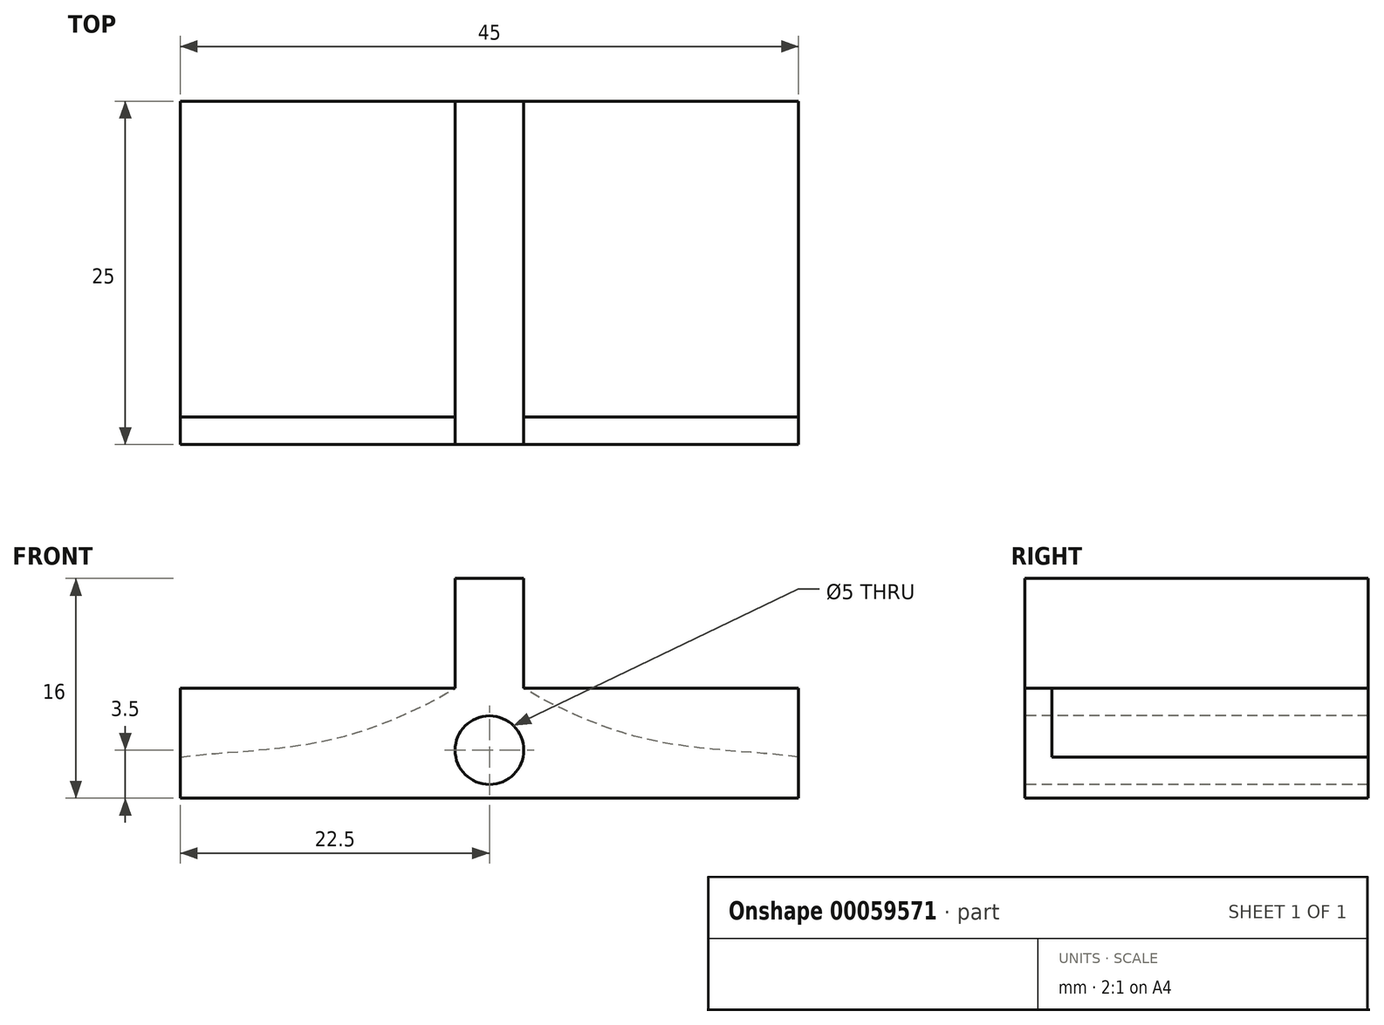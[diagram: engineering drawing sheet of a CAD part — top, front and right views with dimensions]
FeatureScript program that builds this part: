
annotation { "Feature Type Name" : "Feature", "Feature Type Description" : "" }
export const myFeature = defineFeature(function(context is Context, id is Id, definition is map)
    precondition{}
    {
        {
            var Q0;
            Q0=qCreatedBy(makeId("Front.planeOp"),FACE);
            var sketch = newSketch(context, id + "F0", { "sketchPlane" : qUnion([Q0])});
            skLineSegment(sketch, "E0.rect.bottom", {"start": v(-2.5, 8) * mm, "end": v(2.5, 8) * mm});
            skLineSegment(sketch, "E0.rect.top", {"start": v(-2.5, -8) * mm, "end": v(2.5, -8) * mm});
            skLineSegment(sketch, "E0.rect.left", {"start": v(-2.5, 8) * mm, "end": v(-2.5, 0) * mm});
            skLineSegment(sketch, "E0.rect.right", {"start": v(2.5, 8) * mm, "end": v(2.5, 0) * mm});
            skPoint(sketch, "E0.rect.middle", {"position": v(0, 0) * mm});
            skLineSegment(sketch, "E1", {"start": v(2.5, -8) * mm, "end": v(22.5, -8) * mm});
            skLineSegment(sketch, "E2", {"start": v(22.5, -8) * mm, "end": v(22.5, -5) * mm});
            skFitSpline(sketch, "E3", {"points": [v(22.5, -5) * mm, v(11.67, -3.75) * mm, v(2.5, 0) * mm], "startDerivative": vector(-18.47, 2.5) * mm, "endDerivative": vector(-14.83, 8.72) * mm});
            skLineSegment(sketch, "E4.MirrorCS", {"start": v(-2.5, -8) * mm, "end": v(-22.5, -8) * mm});
            skLineSegment(sketch, "E5.MirrorCS", {"start": v(-22.5, -8) * mm, "end": v(-22.5, -5) * mm});
            skFitSpline(sketch, "E6.MirrorCS", {"points": [v(-22.5, -5) * mm, v(-11.67, -3.75) * mm, v(-2.5, 0) * mm], "startDerivative": vector(18.47, 2.5) * mm, "endDerivative": vector(14.83, 8.72) * mm});
            skSolve(sketch);
        }
        {
            var Q0;
            Q0 = qSketchRegion(id + "F0", true);
            extrude(context, id + "F1", {"entities" : qUnion([Q0]), "depth" : 25 * mm});
        }
        {
            var Q0;
            Q0=qCreatedBy(makeId("Top.planeOp"),FACE);
            var sketch = newSketch(context, id + "F2", { "sketchPlane" : qUnion([Q0])});
            skLineSegment(sketch, "E7.bottom", {"start": v(-22.5, -25) * mm, "end": v(22.5, -25) * mm});
            skLineSegment(sketch, "E7.top", {"start": v(-22.5, -23) * mm, "end": v(22.5, -23) * mm});
            skLineSegment(sketch, "E7.left", {"start": v(-22.5, -25) * mm, "end": v(-22.5, -23) * mm});
            skLineSegment(sketch, "E7.right", {"start": v(22.5, -25) * mm, "end": v(22.5, -23) * mm});
            skSolve(sketch);
        }
        {
            var Q0;
            Q0 = qSketchRegion(id + "F2", true);
            extrude(context, id + "F3", {"entities" : qUnion([Q0]), "operationType" : NewBodyOperationType.ADD, "oppositeDirection" : true, "depth" : 8 * mm});
        }
        {
            var Q0;
            Q0=makeQuery(id+"F3.boolean.opBoolean","MERGE",FACE,{"derivedFrom":[makeQuery(id+"F1.opExtrude","CAP_FACE",FACE,{"disambiguationData":[OSD([sQuery(id+"F0.wireOp",EDGE,"E0.rect.bottom"),sQuery(id+"F0.wireOp",EDGE,"E0.rect.top"),sQuery(id+"F0.wireOp",EDGE,"E0.rect.left"),sQuery(id+"F0.wireOp",EDGE,"E0.rect.right"),sQuery(id+"F0.wireOp",EDGE,"E1"),sQuery(id+"F0.wireOp",EDGE,"E2"),sQuery(id+"F0.wireOp",EDGE,"E3"),sQuery(id+"F0.wireOp",EDGE,"E4.MirrorCS"),sQuery(id+"F0.wireOp",EDGE,"E5.MirrorCS"),sQuery(id+"F0.wireOp",EDGE,"E6.MirrorCS")])],"isStart":false}),makeQuery(id+"F3.opExtrude","SWEPT_FACE",FACE,{"disambiguationData":[OSD([sQuery(id+"F2.wireOp",EDGE,"E7.bottom")])]})]});
            var sketch = newSketch(context, id + "F4", { "sketchPlane" : qUnion([Q0])});
            skCircle(sketch, "E8", {"center": v(0, -4.5) * mm, "radius": 2.5 * mm});
            skSolve(sketch);
        }
        {
            var Q0;
            Q0 = qSketchRegion(id + "F4", true);
            extrude(context, id + "F5", {"entities" : qUnion([Q0]), "operationType" : NewBodyOperationType.REMOVE, "endBound" : BoundingType.THROUGH_ALL, "oppositeDirection" : true, "depth" : 25 * mm});
        }
    });
